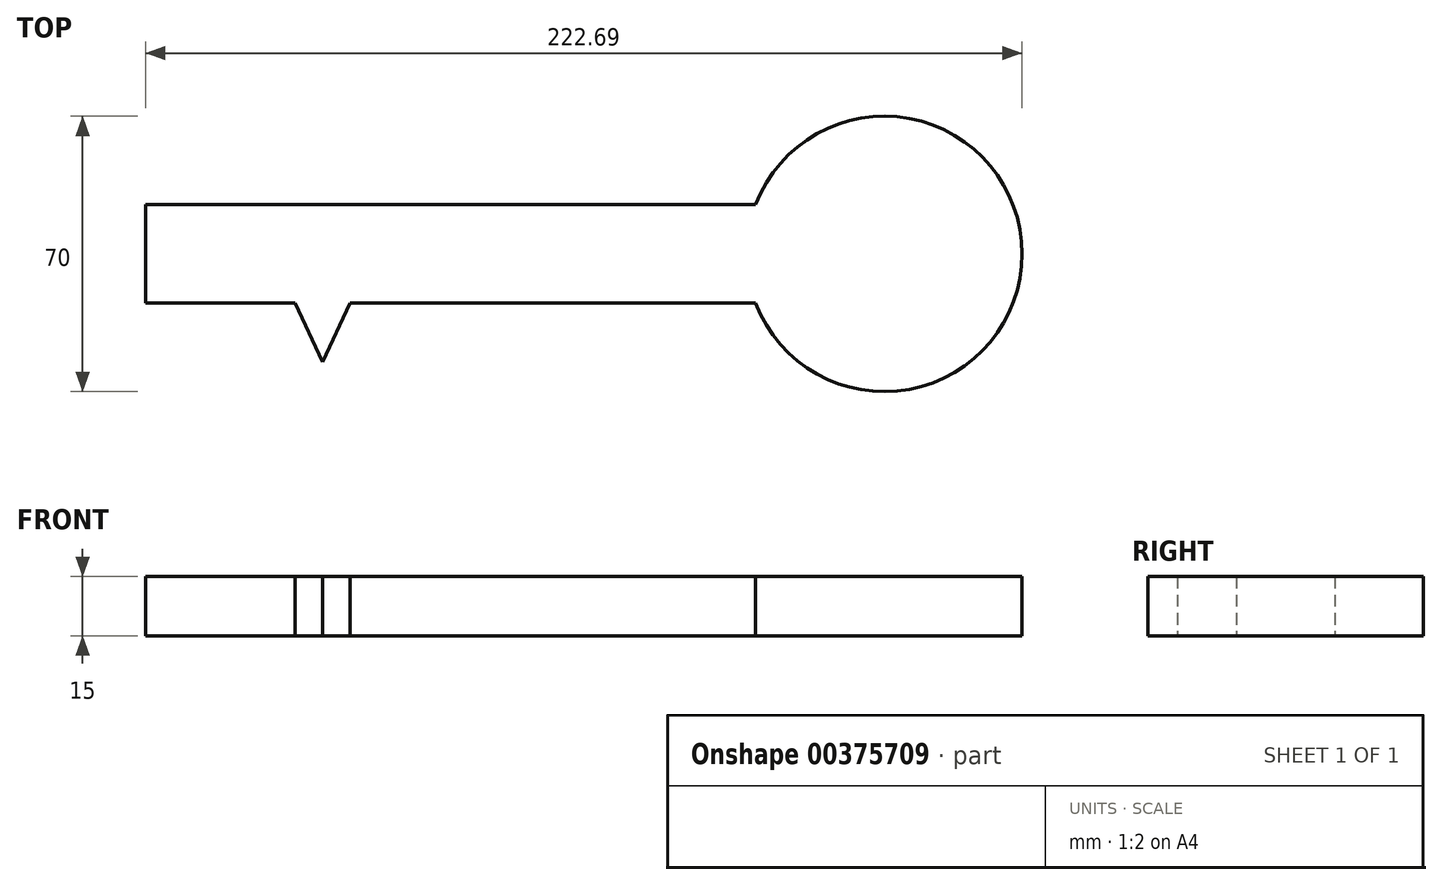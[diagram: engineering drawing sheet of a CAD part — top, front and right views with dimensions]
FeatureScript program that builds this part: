
annotation { "Feature Type Name" : "Feature", "Feature Type Description" : "" }
export const myFeature = defineFeature(function(context is Context, id is Id, definition is map)
    precondition{}
    {
        {
            var Q0;
            Q0=qCreatedBy(makeId("Top.planeOp"),FACE);
            var sketch = newSketch(context, id + "F0", { "sketchPlane" : qUnion([Q0])});
            skLineSegment(sketch, "E0.bottom", {"start": v(-13.85, 25) * mm, "end": v(-168.85, 25) * mm});
            skLineSegment(sketch, "E0.top", {"start": v(-13.85, 0) * mm, "end": v(-168.85, 0) * mm});
            skLineSegment(sketch, "E0.left", {"start": v(-13.85, 25) * mm, "end": v(-13.85, 0) * mm});
            skLineSegment(sketch, "E0.right", {"start": v(-168.85, 25) * mm, "end": v(-168.85, 0) * mm});
            skLineSegment(sketch, "E1.bottom", {"start": v(-168.85, 0) * mm, "end": v(-158.85, 0) * mm});
            skLineSegment(sketch, "E1.top", {"start": v(-168.85, -30) * mm, "end": v(-158.85, -30) * mm});
            skLineSegment(sketch, "E1.left", {"start": v(-168.85, 0) * mm, "end": v(-168.85, -30) * mm});
            skLineSegment(sketch, "E1.right", {"start": v(-158.85, 0) * mm, "end": v(-158.85, -30) * mm});
            skLineSegment(sketch, "E2.bottom", {"start": v(-148.85, 0) * mm, "end": v(-140.85, 0) * mm});
            skLineSegment(sketch, "E2.top", {"start": v(-148.85, -15) * mm, "end": v(-140.85, -15) * mm});
            skLineSegment(sketch, "E2.left", {"start": v(-148.85, 0) * mm, "end": v(-148.85, -15) * mm});
            skLineSegment(sketch, "E2.right", {"start": v(-140.85, 0) * mm, "end": v(-140.85, -15) * mm});
            skLineSegment(sketch, "E3", {"start": v(-130.85, 0) * mm, "end": v(-116.85, 0) * mm});
            skLineSegment(sketch, "E4", {"start": v(-130.85, 0) * mm, "end": v(-130.85, -52.45) * mm});
            skLineSegment(sketch, "E5", {"start": v(-116.85, 0) * mm, "end": v(-116.85, -52.45) * mm});
            skPoint(sketch, "E6.endSnap0", {"position": v(-123.85, 0) * mm});
            skLineSegment(sketch, "E7", {"start": v(-123.85, 0) * mm, "end": v(-123.85, -52.45) * mm});
            skLineSegment(sketch, "E8", {"start": v(-130.85, 0) * mm, "end": v(-123.85, -15) * mm});
            skLineSegment(sketch, "E9", {"start": v(-123.85, -15) * mm, "end": v(-116.85, 0) * mm});
            skPoint(sketch, "E10.startSnap0", {"position": v(-168.85, 12.5) * mm});
            skPoint(sketch, "E10.startSnap1", {"position": v(-91.35, 25) * mm});
            skArc(sketch, "E11", {"start": v(-13.85, 0) * mm, "mid": v(53.84, 12.5) * mm, "end": v(-13.85, 25) * mm});
            skCircle(sketch, "E12", {"center": v(18.84, 12.5) * mm, "radius": 17.5 * mm});
            skLineSegment(sketch, "E13", {"start": v(18.84, 12.5) * mm, "end": v(-168.85, 12.5) * mm, "construction": true});
            skSolve(sketch);
        }
        {
            var Q0;
            Q0=makeQuery(id+"F0.imprint","IMPRINT",FACE,{"disambiguationData":[TD([[makeQuery(id+"F0.imprint","IMPRINT",EDGE,{"derivedFrom":sQuery(id+"F0.wireOp",EDGE,"E0.bottom")}),1.0]])]});
            var Q1;
            Q1=makeQuery(id+"F0.imprint","IMPRINT",FACE,{"disambiguationData":[TD([[makeQuery(id+"F0.imprint","IMPRINT",EDGE,{"derivedFrom":sQuery(id+"F0.wireOp",EDGE,"E1.bottom")}),-1.0]])]});
            var Q2;
            Q2=makeQuery(id+"F0.imprint","IMPRINT",FACE,{"disambiguationData":[TD([[makeQuery(id+"F0.imprint","IMPRINT",EDGE,{"derivedFrom":sQuery(id+"F0.wireOp",EDGE,"E2.bottom")}),-1.0]])]});
            var Q3;
            {var subQ0=sQuery(id+"F0.wireOp",EDGE,"E8");Q3=makeQuery(id+"F0.imprint","IMPRINT",FACE,{"disambiguationData":[TD([[makeQuery(id+"F0.imprint","IMPRINT",EDGE,{"derivedFrom":subQ0}),1.0]])]});}
            var Q4;
            {var subQ0=sQuery(id+"F0.wireOp",EDGE,"E9");Q4=makeQuery(id+"F0.imprint","IMPRINT",FACE,{"disambiguationData":[TD([[makeQuery(id+"F0.imprint","IMPRINT",EDGE,{"derivedFrom":subQ0}),1.0]])]});}
            var Q5;
            Q5=makeQuery(id+"F0.imprint","IMPRINT",FACE,{"disambiguationData":[TD([[makeQuery(id+"F0.imprint","IMPRINT",EDGE,{"derivedFrom":sQuery(id+"F0.wireOp",EDGE,"E0.left")}),1.0]])]});
            var Q6;
            Q6=makeQuery(id+"F0.imprint","IMPRINT",FACE,{"disambiguationData":[TD([[makeQuery(id+"F0.imprint","IMPRINT",EDGE,{"derivedFrom":sQuery(id+"F0.wireOp",EDGE,"E12")}),1.0]])]});
            extrude(context, id + "F1", {"entities" : qUnion([Q0, Q1, Q2, Q3, Q4, Q5, Q6]), "depth" : 15 * mm});
        }
    });
